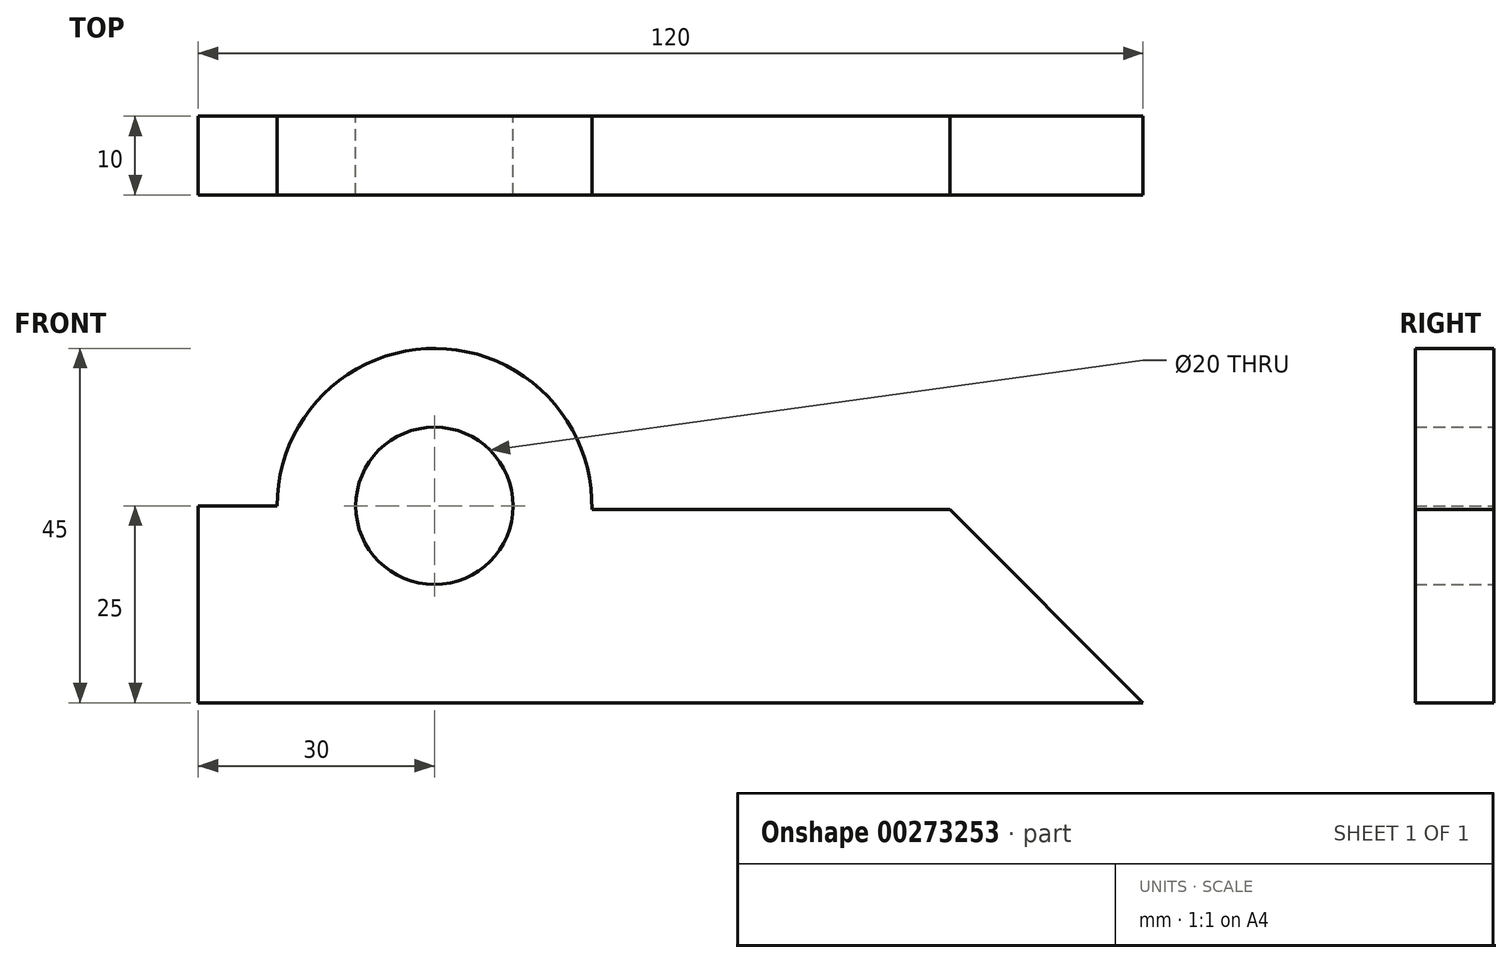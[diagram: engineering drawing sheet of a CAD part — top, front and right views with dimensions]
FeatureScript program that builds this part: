
annotation { "Feature Type Name" : "Feature", "Feature Type Description" : "" }
export const myFeature = defineFeature(function(context is Context, id is Id, definition is map)
    precondition{}
    {
        {
            var Q0;
            Q0=qCreatedBy(makeId("Front.planeOp"),FACE);
            var sketch = newSketch(context, id + "F0", { "sketchPlane" : qUnion([Q0])});
            skLineSegment(sketch, "E0", {"start": v(0, 0) * mm, "end": v(120, 0) * mm});
            skLineSegment(sketch, "E1", {"start": v(120, 0) * mm, "end": v(95.46, 24.54) * mm});
            skLineSegment(sketch, "E2", {"start": v(0, 0) * mm, "end": v(0, 25) * mm});
            skCircle(sketch, "E3", {"center": v(30, 25) * mm, "radius": 10 * mm});
            skArc(sketch, "E4", {"start": v(50, 24.54) * mm, "mid": v(30.23, 45) * mm, "end": v(10, 25) * mm});
            skLineSegment(sketch, "E5", {"start": v(0, 25) * mm, "end": v(10, 25) * mm});
            skLineSegment(sketch, "E6", {"start": v(95.46, 24.54) * mm, "end": v(50, 24.54) * mm});
            skSolve(sketch);
        }
        {
            var Q0;
            Q0 = qSketchRegion(id + "F0", true);
            extrude(context, id + "F1", {"entities" : qUnion([Q0]), "depth" : 10 * mm});
        }
    });
